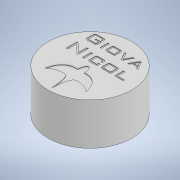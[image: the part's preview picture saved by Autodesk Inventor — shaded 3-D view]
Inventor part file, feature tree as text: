
AUTODESK INVENTOR PART (.ipt)
format: ipt  version: 2021 (Build 250183000, 183)  size: 301,568 bytes
history: native  units: in
note: dims shown in document units (in); Inventor stores cm internally (conversion verified against a paired STEP export)
features: other x2, extrude x1, sketch x1
ambient origin geometry x8: Origin, YZ Plane, XZ Plane, XY Plane, X Axis, Y Axis, Z Axis, Center Point
bodies: Solid1 (feature_tree)
feature tree (4):
  other  "Pastel.stp"
  extrude  "Extrusion1"  [1 undecoded]
  sketch  "Sketch1"  dims[d0=0.3937in d1=0.0in]
  other  "Sólido1"
note: 1 required parameter value undecoded (feature->parameter linkage not recoverable at this tier; creation-order binding heuristic only, values carry confidence <= 0.55)
